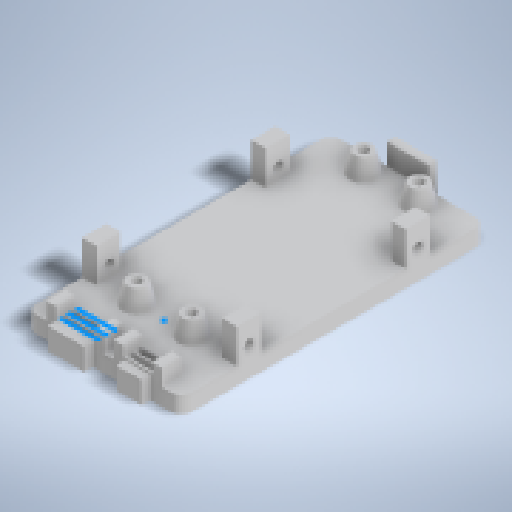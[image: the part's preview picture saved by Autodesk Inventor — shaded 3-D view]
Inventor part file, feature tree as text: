
AUTODESK INVENTOR PART (.ipt)
format: ipt  version: 2023 (Build 270158000, 158)  size: 1,421,824 bytes
history: native  units: in
note: dims shown in document units (in); Inventor stores cm internally (conversion verified against a paired STEP export)
features: extrude x13, sketch x13, projected_geometry x11, other x4, reference x3, plane x2, chamfer x1
ambient origin geometry x8: Origin, YZ Plane, XZ Plane, XY Plane, X Axis, Y Axis, Z Axis, Center Point
bodies: Solid1 (feature_tree)
feature tree (47):
  extrude  "Extrusion1"  Depth=0.0197in
  extrude  "Extrusion2"  Depth=0.0197in
  chamfer  "Chamfer1"  Distance=0.1378in
  extrude  "Extrusion3"  Depth=0.0591in
  extrude  "Extrusion4"  Depth=0.0591in
  extrude  "Extrusion5"  Depth=0.0787in
  extrude  "Extrusion6"  Depth=0.0787in
  extrude  "Extrusion7"  Depth=0.1575in TaperAngle=0.0deg
  sketch  "Sketch8"  dims[d12=0.0591in d13=0.0591in]
  plane  "Work Plane1"
  extrude  "Extrusion8"  Depth=0.1181in
  extrude  "Extrusion9"  Depth=0.1181in
  sketch  "Sketch11"  dims[d16=0.0787in d17=0.0787in]
  plane  "Work Plane2"
  extrude  "Extrusion10"  Depth=0.1969in
  extrude  "Extrusion11"  Depth=0.1181in
  extrude  "Extrusion12"  Depth=0.1969in
  extrude  "Extrusion13"  Depth=0.1181in
  sketch  "Sketch1"  dims[d0=0.0197in d1=0.0197in]
  reference  "Reference1"
  sketch  "Sketch2"  dims[d2=0.0197in d3=0.0197in]
  reference  "Reference2"
  sketch  "Sketch3"  dims[d4=0.0394in]
  sketch  "Sketch4"  dims[d5=0.1969in]
  sketch  "Sketch5"  dims[d6=0.1969in]
  sketch  "Sketch6"  dims[d7=0.3937in d8=0.1378in d9=0.0in]
  sketch  "Sketch7"  dims[d10=0.0787in d11=0.0591in]
  reference  "Reference3"
  sketch  "Sketch10"  dims[d14=0.0591in d15=0.0787in]
  projected_geometry  "Projected Loop1"
  projected_geometry  "Projected Loop2"
  projected_geometry  "Projected Loop3"
  projected_geometry  "Projected Loop4"
  sketch  "Sketch12"  dims[d18=0.0787in d19=0.1575in d20=0.0in]
  projected_geometry  "Projected Loop5"
  projected_geometry  "Projected Loop6"
  projected_geometry  "Projected Loop7"
  projected_geometry  "Projected Loop8"
  sketch  "Sketch13"  dims[d21=0.0394in d22=0.1575in d23=45.0deg d27=0.1181in]
  projected_geometry  "Projected Loop9"
  projected_geometry  "Projected Loop10"
  projected_geometry  "Projected Loop11"
  sketch  "Sketch14"  dims[d28=0.1969in d29=0.1181in d30=0.1969in d31=0.1181in d32=0.1969in d33=0.1181in d34=0.1969in d35=1.1811in d36=2.4803in d37=0.4528in d38=0.1969in d39=0.0in d40=0.0787in d41=0.0984in d42=0.0787in d43=0.0984in d44=1.5719in d45=0.0in d46=0.3937in d47=0.0in d48=0.315in d49=0.1575in d50=0.2362in d51=0.1575in d52=0.0787in d53=0.0787in d54=0.0787in d55=0.0787in d56=0.1575in d57=0.1575in d58=0.1378in d59=0.0in d60=0.0197in d61=0.0197in d62=0.0098in d63=0.0098in d64=0.0098in d65=0.0098in d66=0.0591in d67=0.0in d68=0.0753in d69=0.0in d70=0.1772in d71=0.0in d78=0.0827in d79=0.0in d80=0.0118in d81=0.0118in d82=0.0118in d83=0.0118in d84=0.126in d85=0.0in d86=0.0187in d87=0.0in d88=0.0079in d89=0.0in d72=0.0197in d73=0.0344in]
  parser-record x1  (decoder bookkeeping rows leaked as tree rows — omitted from the tree; the rows remain in map.json)
  other  "Casing.iam"
  other  "Raspberry Pi Pico-R3:1"
  other  "cover:1"
note: 1 file-system path scrubbed to <path> (originals preserved in map.json)
